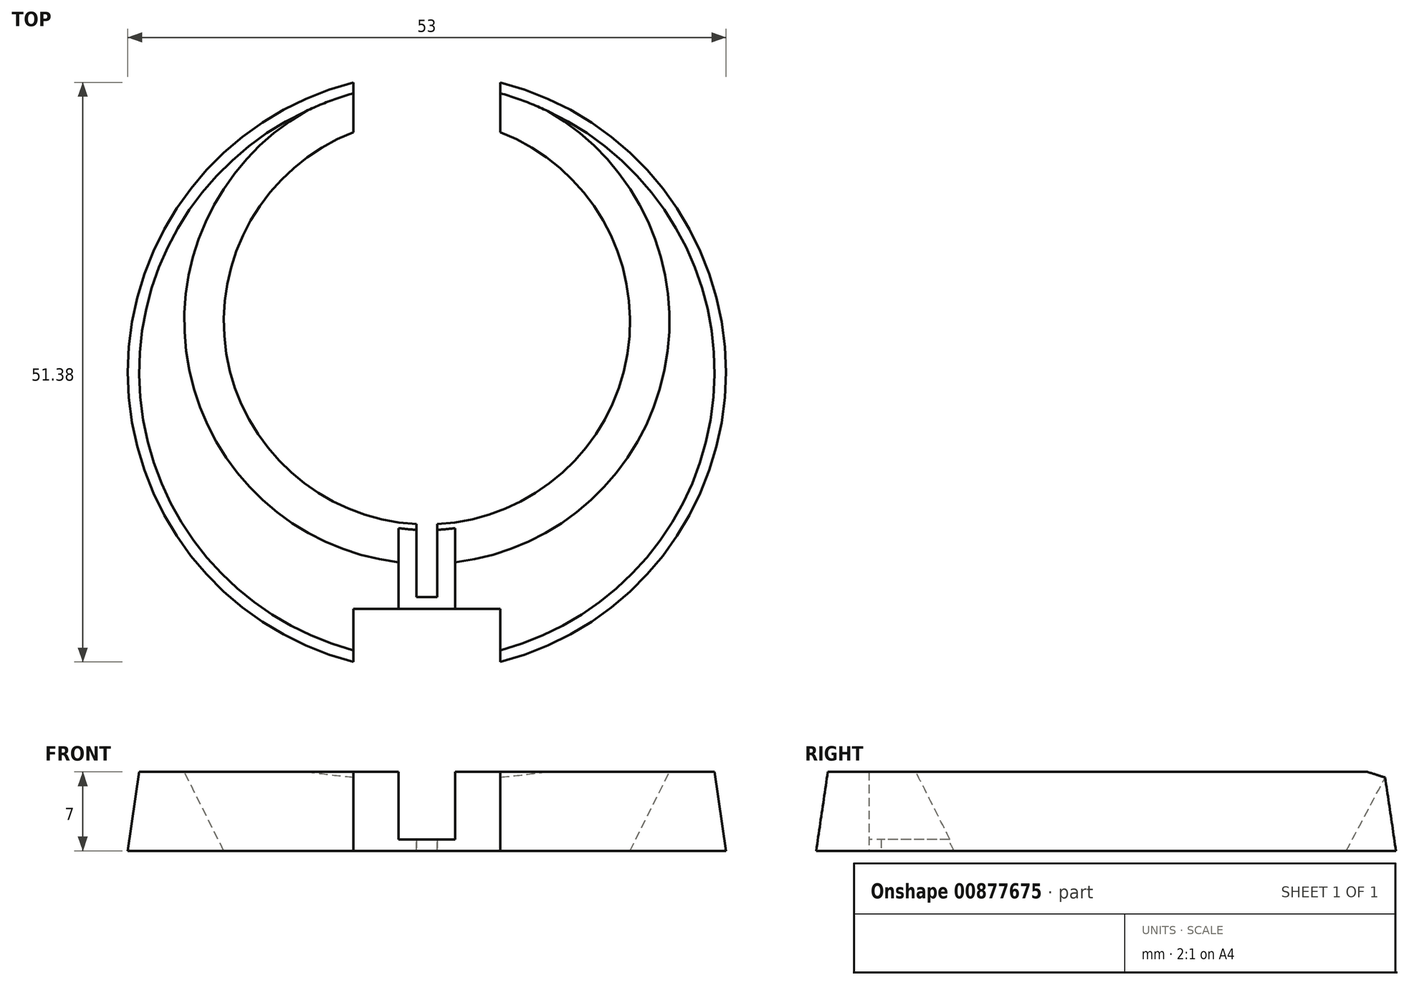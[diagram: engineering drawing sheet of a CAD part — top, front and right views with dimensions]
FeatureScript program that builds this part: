
annotation { "Feature Type Name" : "Feature", "Feature Type Description" : "" }
export const myFeature = defineFeature(function(context is Context, id is Id, definition is map)
    precondition{}
    {
        {
            var Q0;
            Q0=qCreatedBy(makeId("Top.planeOp"),FACE);
            var sketch = newSketch(context, id + "F0", { "sketchPlane" : qUnion([Q0])});
            skCircle(sketch, "E0", {"center": v(0, 0) * mm, "radius": 26.5 * mm});
            skSolve(sketch);
        }
        {
            var Q0;
            Q0=qCreatedBy(makeId("Top.planeOp"),FACE);
            cPlane(context, id + "F1", {"entities" : qUnion([Q0]), "cplaneType" : CPlaneType.OFFSET, "offset" : 7 * mm, "width" : 152.4 * mm, "height" : 152.4 * mm});
        }
        {
            var Q0;
            Q0=qCreatedBy(id+"F1.planeOp",FACE);
            var sketch = newSketch(context, id + "F2", { "sketchPlane" : qUnion([Q0])});
            skCircle(sketch, "E1", {"center": v(0, 0) * mm, "radius": 25.5 * mm});
            skSolve(sketch);
        }
        {
            var Q0;
            Q0=qCreatedBy(id+"F1.planeOp",FACE);
            var sketch = newSketch(context, id + "F3", { "sketchPlane" : qUnion([Q0])});
            skCircle(sketch, "E2", {"center": v(0, 4.5) * mm, "radius": 21.5 * mm});
            skSolve(sketch);
        }
        {
            var Q0;
            Q0=qCreatedBy(makeId("Top.planeOp"),FACE);
            var sketch = newSketch(context, id + "F4", { "sketchPlane" : qUnion([Q0])});
            skCircle(sketch, "E3", {"center": v(0, 4.5) * mm, "radius": 18 * mm});
            skSolve(sketch);
        }
        {
            var Q0;
            Q0=makeQuery(id+"F0.imprint","IMPRINT",FACE,{"disambiguationData":[TD([[makeQuery(id+"F0.imprint","IMPRINT",EDGE,{"derivedFrom":sQuery(id+"F0.wireOp",EDGE,"E0")}),1.0]])]});
            var Q1;
            Q1=makeQuery(id+"F2.imprint","IMPRINT",FACE,{"disambiguationData":[TD([[makeQuery(id+"F2.imprint","IMPRINT",EDGE,{"derivedFrom":sQuery(id+"F2.wireOp",EDGE,"E1")}),1.0]])]});
            loft(context, id + "F5", {"sheetProfilesArray" : [{ "sheetProfileEntities" : qUnion([Q0]) }, { "sheetProfileEntities" : qUnion([Q1]) }]});
        }
        {
            var Q1;
            Q1=makeQuery(id+"F4.imprint","IMPRINT",FACE,{"disambiguationData":[TD([[makeQuery(id+"F4.imprint","IMPRINT",EDGE,{"derivedFrom":sQuery(id+"F4.wireOp",EDGE,"E3")}),1.0]])]});
            var Q2;
            Q2=makeQuery(id+"F3.imprint","IMPRINT",FACE,{"disambiguationData":[TD([[makeQuery(id+"F3.imprint","IMPRINT",EDGE,{"derivedFrom":sQuery(id+"F3.wireOp",EDGE,"E2")}),1.0]])]});
            loft(context, id + "F6", {"operationType" : NewBodyOperationType.REMOVE, "sheetProfilesArray" : [{ "sheetProfileEntities" : qUnion([Q1]) }, { "sheetProfileEntities" : qUnion([Q2]) }]});
        }
        {
            var Q0;
            Q0=qCreatedBy(makeId("Top.planeOp"),FACE);
            var sketch = newSketch(context, id + "F7", { "sketchPlane" : qUnion([Q0])});
            skLineSegment(sketch, "E4.bottom", {"start": v(-6.5, 0) * mm, "end": v(6.5, 0) * mm});
            skLineSegment(sketch, "E4.top", {"start": v(-6.5, 32.7) * mm, "end": v(6.5, 32.7) * mm});
            skLineSegment(sketch, "E4.left", {"start": v(-6.5, 0) * mm, "end": v(-6.5, 32.7) * mm});
            skLineSegment(sketch, "E4.right", {"start": v(6.5, 0) * mm, "end": v(6.5, 32.7) * mm});
            skLineSegment(sketch, "E5.bottom", {"start": v(-6.5, -30) * mm, "end": v(6.5, -30) * mm});
            skLineSegment(sketch, "E5.top", {"start": v(-6.5, -21) * mm, "end": v(6.5, -21) * mm});
            skLineSegment(sketch, "E5.left", {"start": v(-6.5, -30) * mm, "end": v(-6.5, -21) * mm});
            skLineSegment(sketch, "E5.right", {"start": v(6.5, -30) * mm, "end": v(6.5, -21) * mm});
            skLineSegment(sketch, "E6.bottom", {"start": v(-2.5, -11.47) * mm, "end": v(2.5, -11.47) * mm});
            skLineSegment(sketch, "E6.top", {"start": v(-2.5, -21) * mm, "end": v(2.5, -21) * mm});
            skLineSegment(sketch, "E6.left", {"start": v(-2.5, -11.47) * mm, "end": v(-2.5, -21) * mm});
            skLineSegment(sketch, "E6.right", {"start": v(2.5, -11.47) * mm, "end": v(2.5, -21) * mm});
            skLineSegment(sketch, "E7.bottom", {"start": v(-0.91, -8.12) * mm, "end": v(0.91, -8.12) * mm});
            skLineSegment(sketch, "E7.top", {"start": v(-0.91, -19.93) * mm, "end": v(0.91, -19.93) * mm});
            skLineSegment(sketch, "E7.left", {"start": v(-0.91, -8.12) * mm, "end": v(-0.91, -19.93) * mm});
            skLineSegment(sketch, "E7.right", {"start": v(0.91, -8.12) * mm, "end": v(0.91, -19.93) * mm});
            skSolve(sketch);
        }
        {
            var Q0;
            Q0=makeQuery(id+"F7.imprint","IMPRINT",FACE,{"disambiguationData":[TD([[makeQuery(id+"F7.imprint","IMPRINT",EDGE,{"derivedFrom":sQuery(id+"F7.wireOp",EDGE,"E4.bottom")}),1.0]])]});
            var Q1;
            Q1=makeQuery(id+"F7.imprint","IMPRINT",FACE,{"disambiguationData":[TD([[makeQuery(id+"F7.imprint","IMPRINT",EDGE,{"derivedFrom":sQuery(id+"F7.wireOp",EDGE,"E5.bottom")}),1.0]])]});
            extrude(context, id + "F8", {"entities" : qUnion([Q0, Q1]), "operationType" : NewBodyOperationType.REMOVE, "depth" : 25 * mm, "offsetDistance" : 25 * mm});
        }
        {
            var Q0;
            Q0=makeQuery(id+"F7.imprint","IMPRINT",FACE,{"disambiguationData":[TD([[makeQuery(id+"F7.imprint","IMPRINT",EDGE,{"derivedFrom":sQuery(id+"F7.wireOp",EDGE,"E6.bottom")}),-1.0]])]});
            extrude(context, id + "F9", {"entities" : qUnion([Q0]), "operationType" : NewBodyOperationType.REMOVE, "depth" : 25 * mm, "offsetDistance" : 25 * mm, "hasSecondDirection" : true, "secondDirectionOppositeDirection" : false, "secondDirectionDepth" : 1 * mm});
        }
        {
            var Q0;
            {var subQ5=sQuery(id+"F7.wireOp",EDGE,"E7.top");Q0=makeQuery(id+"F7.imprint","IMPRINT",FACE,{"disambiguationData":[TD([[makeQuery(id+"F7.imprint","IMPRINT",EDGE,{"derivedFrom":subQ5}),1.0]])]});}
            extrude(context, id + "F10", {"entities" : qUnion([Q0]), "operationType" : NewBodyOperationType.REMOVE, "depth" : 25 * mm, "offsetDistance" : 25 * mm});
        }
    });
